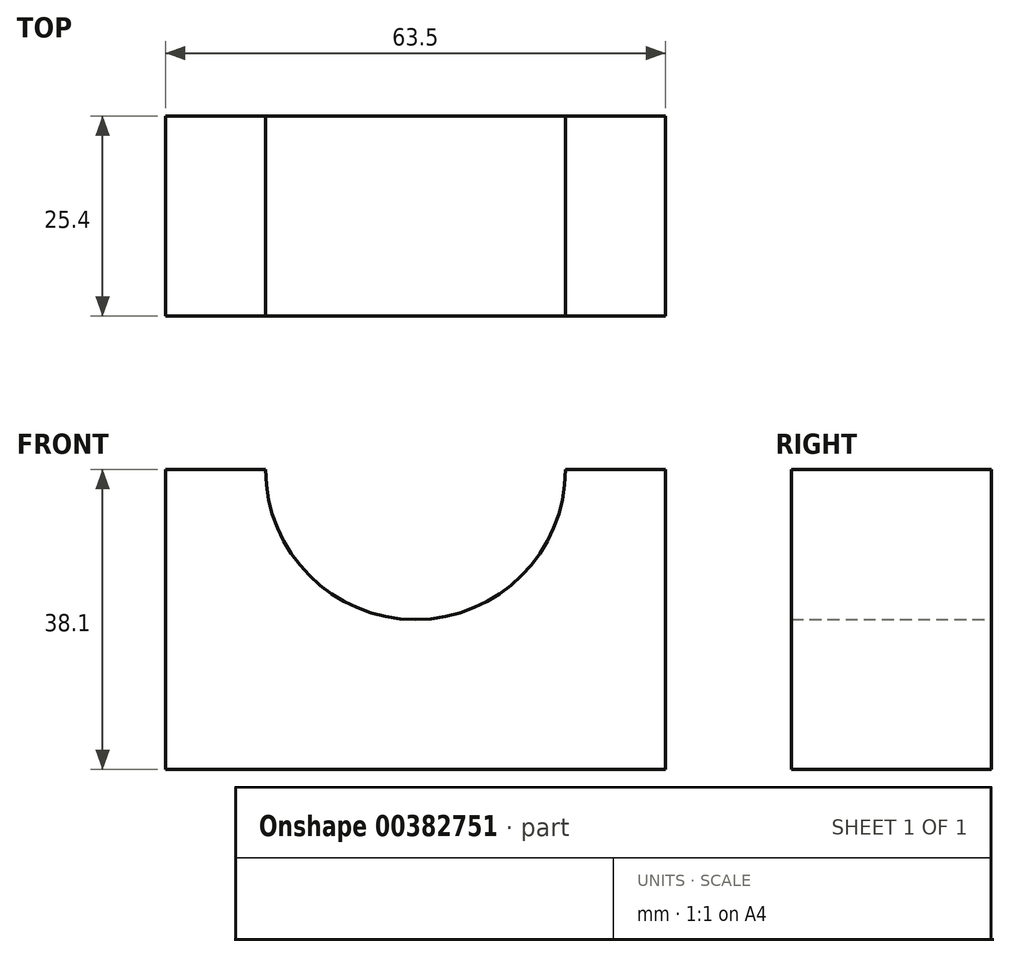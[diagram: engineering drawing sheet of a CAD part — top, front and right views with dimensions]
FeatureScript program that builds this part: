
annotation { "Feature Type Name" : "Feature", "Feature Type Description" : "" }
export const myFeature = defineFeature(function(context is Context, id is Id, definition is map)
    precondition{}
    {
        {
            var Q0;
            Q0=qCreatedBy(makeId("Front.planeOp"),FACE);
            var sketch = newSketch(context, id + "F0", { "sketchPlane" : qUnion([Q0])});
            skLineSegment(sketch, "E0.bottom", {"start": v(0, 0) * mm, "end": v(63.5, 0) * mm});
            skLineSegment(sketch, "E0.top", {"start": v(0, 38.1) * mm, "end": v(63.5, 38.1) * mm});
            skLineSegment(sketch, "E0.left", {"start": v(0, 0) * mm, "end": v(0, 38.1) * mm});
            skLineSegment(sketch, "E0.right", {"start": v(63.5, 0) * mm, "end": v(63.5, 38.1) * mm});
            skArc(sketch, "E1", {"start": v(12.7, 38.1) * mm, "mid": v(31.75, 19.05) * mm, "end": v(50.8, 38.1) * mm});
            skSolve(sketch);
        }
        {
            var Q0;
            Q0=makeQuery(id+"F0.imprint","IMPRINT",FACE,{"disambiguationData":[TD([[makeQuery(id+"F0.imprint","IMPRINT",EDGE,{"derivedFrom":sQuery(id+"F0.wireOp",EDGE,"E0.bottom")}),1.0]])]});
            extrude(context, id + "F1", {"entities" : qUnion([Q0]), "depth" : 25.4 * mm});
        }
    });
